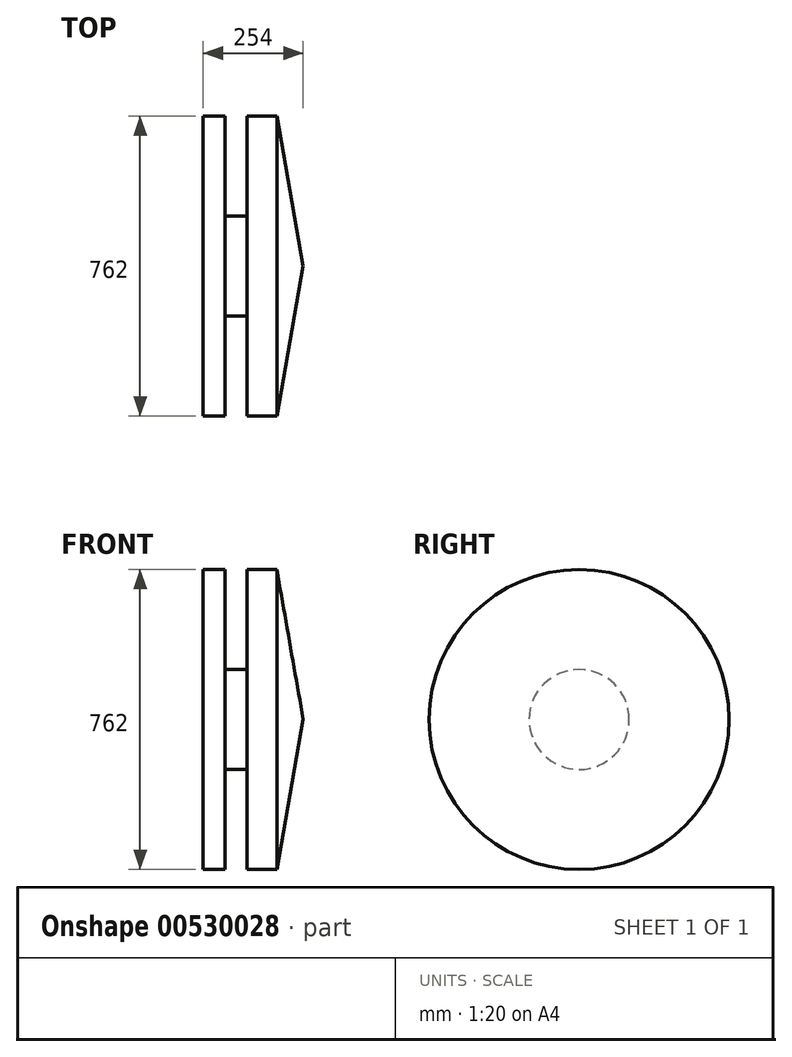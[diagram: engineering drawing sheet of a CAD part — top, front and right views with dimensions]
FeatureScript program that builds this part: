
annotation { "Feature Type Name" : "Feature", "Feature Type Description" : "" }
export const myFeature = defineFeature(function(context is Context, id is Id, definition is map)
    precondition{}
    {
        {
            var Q0;
            Q0=qCreatedBy(makeId("Front.planeOp"),FACE);
            var sketch = newSketch(context, id + "F0", { "sketchPlane" : qUnion([Q0])});
            skLineSegment(sketch, "E0", {"start": v(-104.2, 254) * mm, "end": v(-104.2, -127) * mm});
            skLineSegment(sketch, "E1", {"start": v(-104.2, -127) * mm, "end": v(149.8, -127) * mm});
            skLineSegment(sketch, "E2", {"start": v(149.8, -127) * mm, "end": v(82.61, 254) * mm});
            skLineSegment(sketch, "E3", {"start": v(82.61, 254) * mm, "end": v(6.41, 254) * mm});
            skLineSegment(sketch, "E4", {"start": v(6.41, 254) * mm, "end": v(6.41, 0) * mm});
            skLineSegment(sketch, "E5", {"start": v(6.41, 0) * mm, "end": v(-49.39, 0) * mm});
            skLineSegment(sketch, "E6", {"start": v(-49.39, 0) * mm, "end": v(-49.39, 254) * mm});
            skLineSegment(sketch, "E7", {"start": v(-49.39, 254) * mm, "end": v(-104.2, 254) * mm});
            skSolve(sketch);
        }
        {
            var Q0;
            Q0=makeQuery(id+"F0.imprint","IMPRINT",FACE,{"disambiguationData":[TD([[makeQuery(id+"F0.imprint","IMPRINT",EDGE,{"derivedFrom":sQuery(id+"F0.wireOp",EDGE,"E0")}),1.0]])]});
            var Q1;
            Q1=sQuery(id+"F0.wireOp",EDGE,"E1");
            revolve(context, id + "F1", {"entities" : qUnion([Q0]), "axis" : qUnion([Q1]), "revolveType" : RevolveType.FULL});
        }
    });
